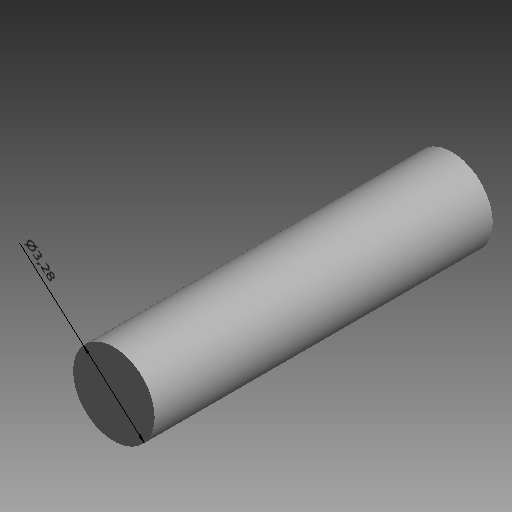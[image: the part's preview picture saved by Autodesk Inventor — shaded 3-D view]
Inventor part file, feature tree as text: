
AUTODESK INVENTOR PART (.ipt)
format: ipt  version: 2019 (Build 230136000, 136)  size: 95,232 bytes
history: native  units: mm (DEFAULTED — no unit token found)
features: revolve x1, sketch x1, other x1
ambient origin geometry x8: Origin, YZ Plane, XZ Plane, XY Plane, X Axis, Y Axis, Z Axis, Center Point
bodies: Solid1 (feature_tree), Body2_1_XY (feature_tree), Body2_1_YZ (feature_tree), Body2_1_ZX (feature_tree), Body2_1_X (feature_tree), Body2_1_Y (feature_tree), Body2_1_Z (feature_tree), Body2_1_Center (feature_tree)
feature tree (3):
  revolve  "Revolution1"  [1 undecoded]
  sketch  "Sketch_1"  dims[d0=360.0deg d1=55.569354mm d2=3.28mm]
  other  "直径寸法 1"
note: 1 required parameter value undecoded (feature->parameter linkage not recoverable at this tier; creation-order binding heuristic only, values carry confidence <= 0.55)
